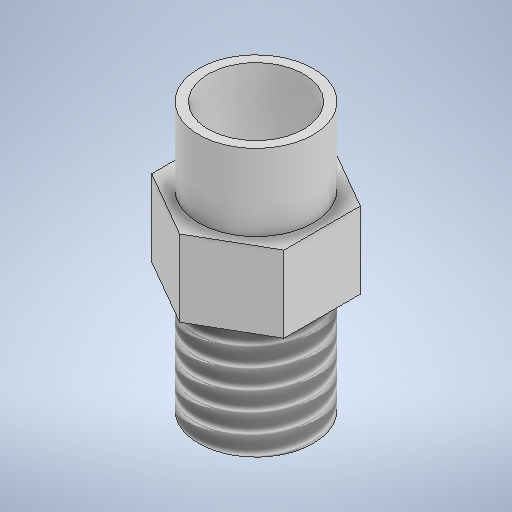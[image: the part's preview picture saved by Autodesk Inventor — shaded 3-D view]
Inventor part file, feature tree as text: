
AUTODESK INVENTOR PART (.ipt)
format: ipt  version: 2025.1 (Build 291241000, 241)  size: 284,672 bytes
history: native  units: mm
features: sketch x4, extrude x3, hole x1, thread x1
ambient origin geometry x8: Origin, YZ Plane, XZ Plane, XY Plane, X Axis, Y Axis, Z Axis, Center Point
bodies: Solid1 (feature_tree)
feature tree (9):
  extrude  "Extrusion1"  Depth=4.0mm TaperAngle=0.0deg
  extrude  "Extrusion2"  Depth=4.0mm TaperAngle=0.0deg
  extrude  "Extrusion3"  Depth=6.0mm TaperAngle=0.0deg
  hole  "Hole1"  [1 undecoded]
  thread  "Thread1"  [1 undecoded]
  sketch  "Sketch2"  dims[d0=8.0mm d1=4.0mm d2=0.0mm]
  sketch  "Sketch3"  dims[d3=6.0mm d4=4.0mm d5=0.0mm]
  sketch  "Sketch4"  dims[d6=6.0mm d7=6.0mm d8=0.0mm]
  sketch  "Sketch5"  dims[d9=5.0mm d10=5.0mm d11=4.0mm d12=2.0mm d13=90.0deg d14=8.0mm d15=20.594885mm d16=35.9mm d17=0.0mm]
note: 2 required parameter values undecoded (feature->parameter linkage not recoverable at this tier; creation-order binding heuristic only, values carry confidence <= 0.55)
